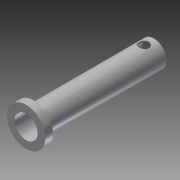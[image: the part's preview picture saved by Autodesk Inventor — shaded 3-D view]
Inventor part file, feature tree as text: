
AUTODESK INVENTOR PART (.ipt)
format: ipt  version: 2013 (Build 170138000, 138)  size: 109,056 bytes
history: native  units: in
note: dims shown in document units (in); Inventor stores cm internally (conversion verified against a paired STEP export)
features: sketch x4, extrude x3, plane x2
ambient origin geometry x8: Origin, YZ Plane, XZ Plane, XY Plane, X Axis, Y Axis, Z Axis, Center Point
bodies: Solid1 (feature_tree)
feature tree (9):
  extrude  "Extrusion1"  Depth=0.45in
  extrude  "Extrusion2"  Depth=0.75in
  sketch  "Sketch3"  dims[d5=0.15in d6=0.0in d7=90.0deg d8=0.25in]
  plane  "Work Plane2"
  extrude  "Extrusion3"  Depth=0.25in TaperAngle=90.0deg
  sketch  "Sketch1"  dims[d0=0.5in d1=0.45in]
  sketch  "Sketch2"  dims[d2=2.5in d3=0.0in d4=0.75in]
  plane  "Work Plane1"
  sketch  "Sketch4"  dims[d9=0.2in d10=0.2in d11=2.0in d12=0.0in]
